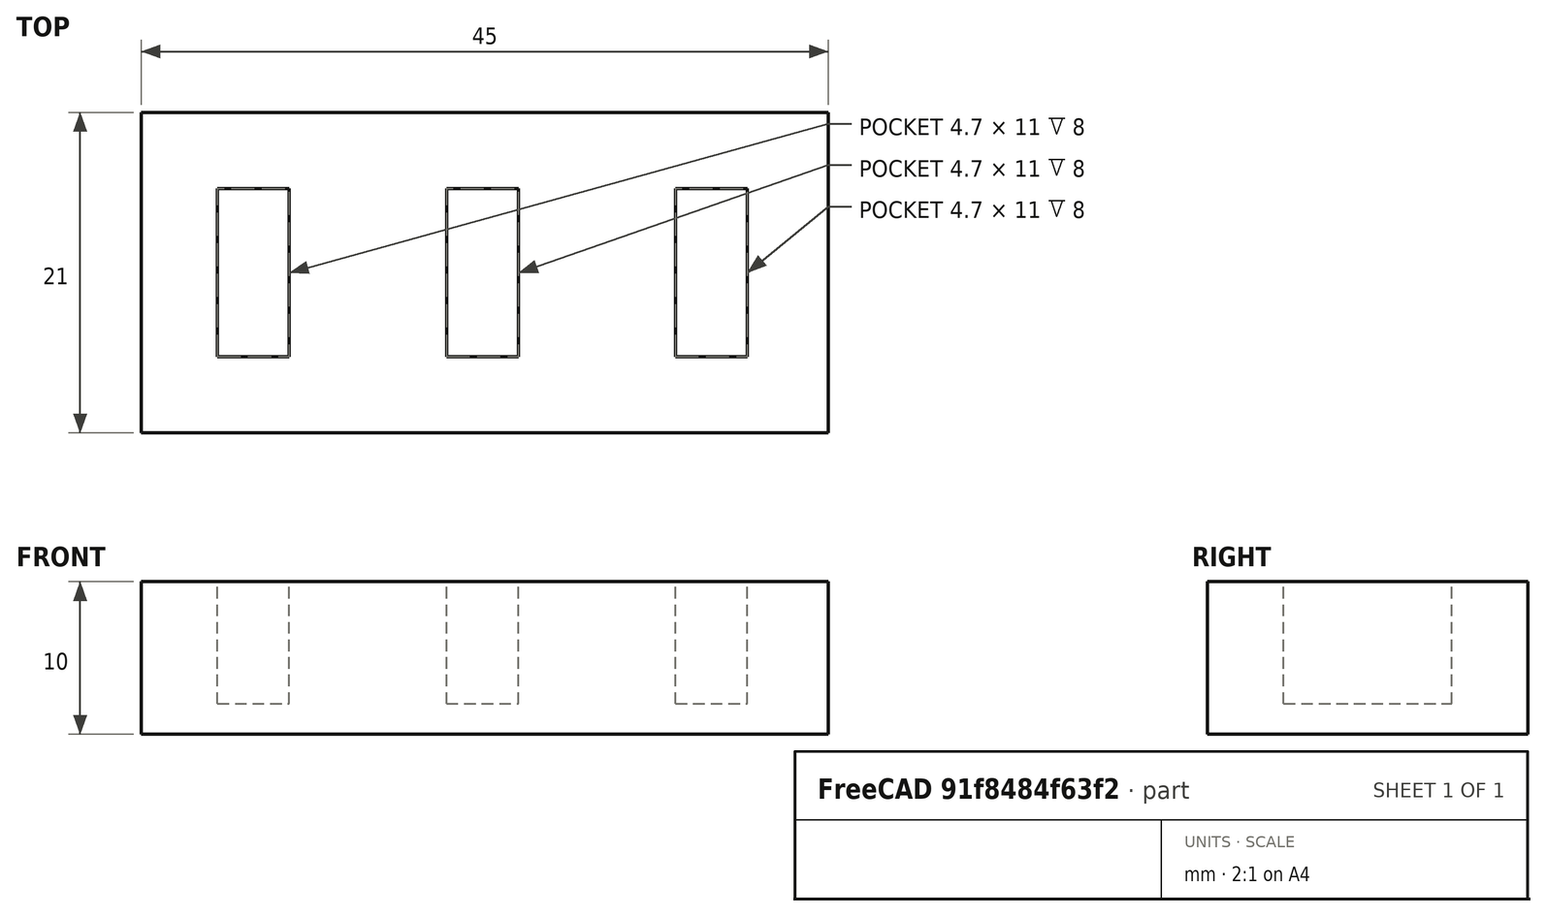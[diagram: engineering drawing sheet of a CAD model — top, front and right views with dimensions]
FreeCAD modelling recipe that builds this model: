
FCSTD DOCUMENT  (FreeCAD 0.21R33694 (Git))
Label: OJT1_T08P07_porta_pendrivers
License: All rights reserved
LicenseURL: http://en.wikipedia.org/wiki/All_rights_reserved
objects: Part::Box×4, Part::MultiFuse×1, Part::Cut×1
note: 6 computed .brp shape members not serialized (recipe doc carries the construction recipe); baked Part::Feature solids carry a one-line shape summary decoded from their .brp

FEATURE [Part::Box] Box  label="ranura1"
  AttacherType = Attacher::AttachEngine3D
  Height = 12
  Length = 4.7
  Width = 11
FEATURE [Part::Box] Box001  label="ranura2"
  AttacherType = Attacher::AttachEngine3D
  Height = 12
  Length = 4.7
  Placement = pos=(15,0,0) rot=(0,0,1;0rad)
  Width = 11
FEATURE [Part::Box] Box002  label="ranura3"
  AttacherType = Attacher::AttachEngine3D
  Height = 12
  Length = 4.7
  Placement = pos=(30,0,0) rot=(0,0,1;0rad)
  Width = 11
FEATURE [Part::MultiFuse] Fusion  label="ranuras"
  Placement = pos=(5,5,2) rot=(0,0,1;0rad)
  Refine = true
  Shapes = -> [Box,Box001,Box002]
FEATURE [Part::Box] Box003  label="base"
  AttacherType = Attacher::AttachEngine3D
  Height = 10
  Length = 45
  Width = 21
FEATURE [Part::Cut] Cut
  Base = -> Box003
  Refine = true
  Tool = -> Fusion
